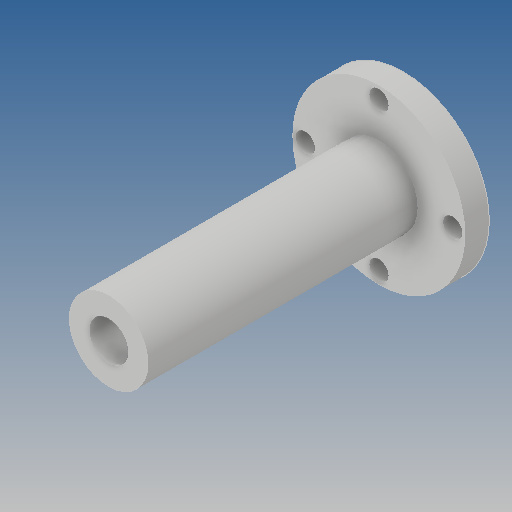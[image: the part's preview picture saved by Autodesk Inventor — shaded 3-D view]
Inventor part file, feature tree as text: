
AUTODESK INVENTOR PART (.ipt)
format: ipt  version: 2018 (Build 220112000, 112)  size: 140,800 bytes
history: native  units: mm
features: extrude x3, sketch x3, other x1
ambient origin geometry x8: Origin, YZ Plane, XZ Plane, XY Plane, X Axis, Y Axis, Z Axis, Center Point
bodies: Solid1 (feature_tree)
feature tree (7):
  other  "<userpath>\OneDrive\Objet3D\3DPrinter\Parameters.xlsx"
  extrude  "Extrusion1"  Depth=8.0mm
  extrude  "Extrusion2"  Depth=5.0mm
  extrude  "Extrusion3"  Depth=55.0mm
  sketch  "Sketch3"  dims[d0=8.0mm d1=35.0mm]
  sketch  "Sketch4"  dims[d2=5.0mm d3=0.0mm d4=16.0mm]
  sketch  "Sketch5"  dims[d5=8.0mm d6=55.0mm d7=0.0mm d8=4.0mm d9=15.0mm d10=15.0mm d11=15.0mm d12=15.0mm d13=4.0mm d14=4.0mm d15=4.0mm d16=55.0mm d17=0.0mm]
